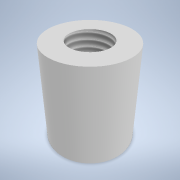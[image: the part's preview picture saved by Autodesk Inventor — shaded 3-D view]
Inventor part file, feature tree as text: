
AUTODESK INVENTOR PART (.ipt)
format: ipt  version: 2020 (Build 240168000, 168)  size: 102,912 bytes
history: native  units: mm
features: thread x2, other x1, extrude x1, sketch x1
ambient origin geometry x8: Origin, YZ Plane, XZ Plane, XY Plane, X Axis, Y Axis, Z Axis, Center Point
bodies: Body1 (feature_tree)
feature tree (5):
  other  "Твердое тело1"
  extrude  "Выдавливание1"  Depth=3.0mm
  thread  "Резьба4"
  thread  "Резьба5"
  sketch  "Эскиз1"
